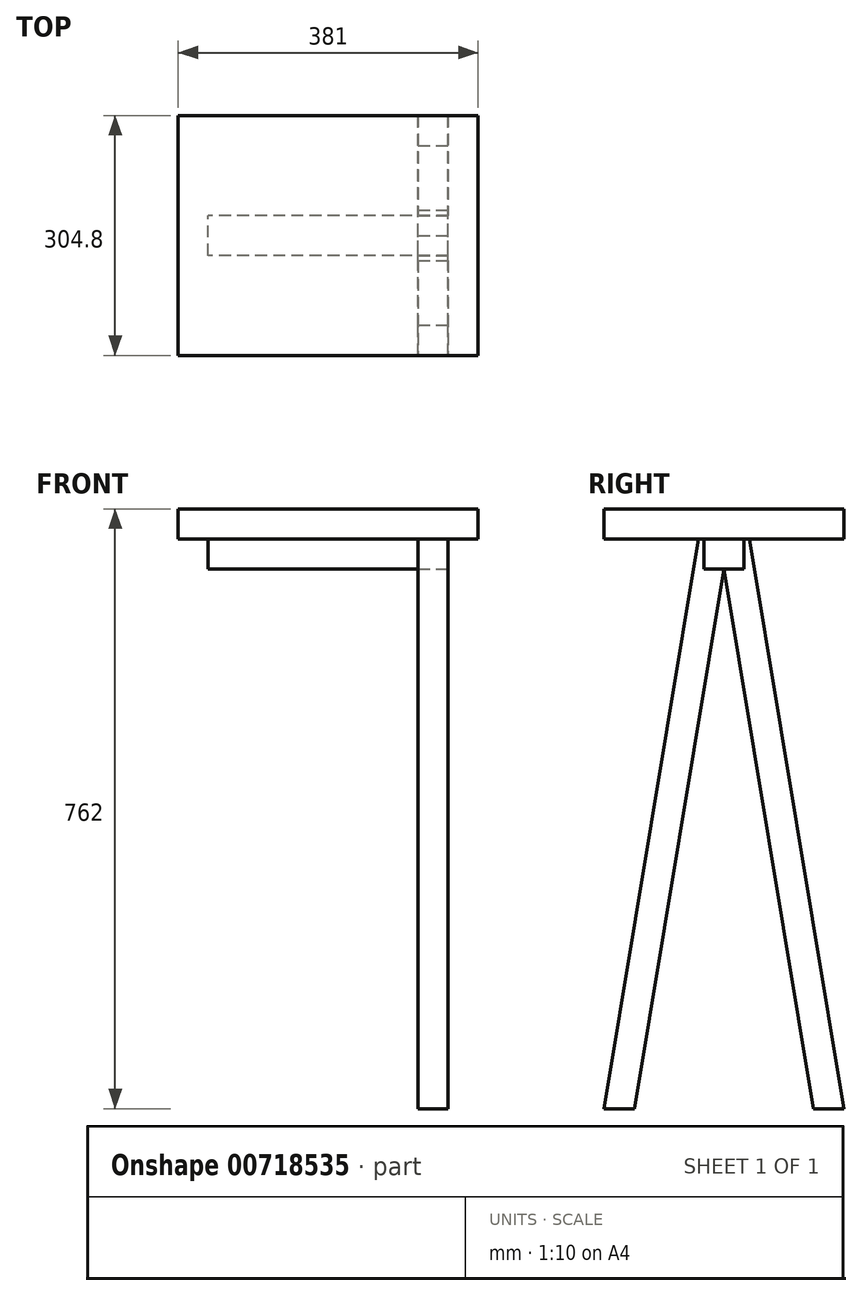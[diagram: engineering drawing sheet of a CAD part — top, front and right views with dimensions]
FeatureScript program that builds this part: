
annotation { "Feature Type Name" : "Feature", "Feature Type Description" : "" }
export const myFeature = defineFeature(function(context is Context, id is Id, definition is map)
    precondition{}
    {
        {
            var Q0;
            Q0=qCreatedBy(makeId("Top.planeOp"),FACE);
            var sketch = newSketch(context, id + "F0", { "sketchPlane" : qUnion([Q0])});
            skLineSegment(sketch, "E0.bottom", {"start": v(0, 0) * mm, "end": v(381, 0) * mm});
            skLineSegment(sketch, "E0.top", {"start": v(0, 304.8) * mm, "end": v(381, 304.8) * mm});
            skLineSegment(sketch, "E0.left", {"start": v(0, 0) * mm, "end": v(0, 304.8) * mm});
            skLineSegment(sketch, "E0.right", {"start": v(381, 0) * mm, "end": v(381, 304.8) * mm});
            skSolve(sketch);
        }
        {
            var Q0;
            Q0=makeQuery(id+"F0.imprint","IMPRINT",FACE,{"disambiguationData":[TD([[makeQuery(id+"F0.imprint","IMPRINT",EDGE,{"derivedFrom":sQuery(id+"F0.wireOp",EDGE,"E0.bottom")}),1.0]])]});
            extrude(context, id + "F1", {"entities" : qUnion([Q0]), "depth" : 38.1 * mm, "offsetDistance" : 25.4 * mm});
        }
        {
            var Q0;
            Q0=makeQuery(id+"F1.opExtrude","CAP_FACE",FACE,{"disambiguationData":[OSD([sQuery(id+"F0.wireOp",EDGE,"E0.bottom"),sQuery(id+"F0.wireOp",EDGE,"E0.top"),sQuery(id+"F0.wireOp",EDGE,"E0.left"),sQuery(id+"F0.wireOp",EDGE,"E0.right")])],"isStart":true});
            var sketch = newSketch(context, id + "F2", { "sketchPlane" : qUnion([Q0])});
            skLineSegment(sketch, "E1.bottom", {"start": v(342.9, -127) * mm, "end": v(38.1, -127) * mm});
            skLineSegment(sketch, "E1.top", {"start": v(342.9, -177.8) * mm, "end": v(38.1, -177.8) * mm});
            skLineSegment(sketch, "E1.left", {"start": v(342.9, -127) * mm, "end": v(342.9, -177.8) * mm});
            skLineSegment(sketch, "E1.right", {"start": v(38.1, -127) * mm, "end": v(38.1, -177.8) * mm});
            skLineSegment(sketch, "E2", {"start": v(190.5, 0) * mm, "end": v(190.5, -127) * mm, "construction": true});
            skLineSegment(sketch, "E3", {"start": v(190.5, -304.8) * mm, "end": v(190.5, -177.8) * mm, "construction": true});
            skSolve(sketch);
        }
        {
            var Q0;
            Q0 = qSketchRegion(id + "F2", true);
            extrude(context, id + "F3", {"entities" : qUnion([Q0]), "depth" : 38.1 * mm, "offsetDistance" : 25.4 * mm});
        }
        {
            var Q0;
            Q0=makeQuery(id+"F3.opExtrude","SWEPT_FACE",FACE,{"disambiguationData":[OSD([sQuery(id+"F2.wireOp",EDGE,"E1.left")])]});
            var sketch = newSketch(context, id + "F4", { "sketchPlane" : qUnion([Q0])});
            skLineSegment(sketch, "E4", {"start": v(120.1, 0) * mm, "end": v(0, -723.9) * mm});
            skLineSegment(sketch, "E5", {"start": v(0, -723.9) * mm, "end": v(38.62, -723.9) * mm});
            skLineSegment(sketch, "E6", {"start": v(38.62, -723.9) * mm, "end": v(152.4, -38.1) * mm});
            skLineSegment(sketch, "E7", {"start": v(152.4, -38.1) * mm, "end": v(127, -38.1) * mm});
            skLineSegment(sketch, "E8", {"start": v(127, -38.1) * mm, "end": v(127, 0) * mm});
            skLineSegment(sketch, "E9", {"start": v(120.1, 0) * mm, "end": v(127, 0) * mm});
            skLineSegment(sketch, "E10", {"start": v(152.4, -38.1) * mm, "end": v(266.18, -723.9) * mm});
            skLineSegment(sketch, "E11", {"start": v(266.18, -723.9) * mm, "end": v(304.8, -723.9) * mm});
            skLineSegment(sketch, "E12", {"start": v(304.8, -723.9) * mm, "end": v(184.7, 0) * mm});
            skLineSegment(sketch, "E13", {"start": v(184.7, 0) * mm, "end": v(177.8, 0) * mm});
            skLineSegment(sketch, "E14", {"start": v(177.8, 0) * mm, "end": v(177.8, -38.1) * mm});
            skLineSegment(sketch, "E15", {"start": v(177.8, -38.1) * mm, "end": v(152.4, -38.1) * mm});
            skSolve(sketch);
        }
        {
            var Q0;
            Q0 = qSketchRegion(id + "F4", true);
            extrude(context, id + "F5", {"entities" : qUnion([Q0]), "oppositeDirection" : true, "depth" : 38.1 * mm, "offsetDistance" : 25.4 * mm});
        }
    });
